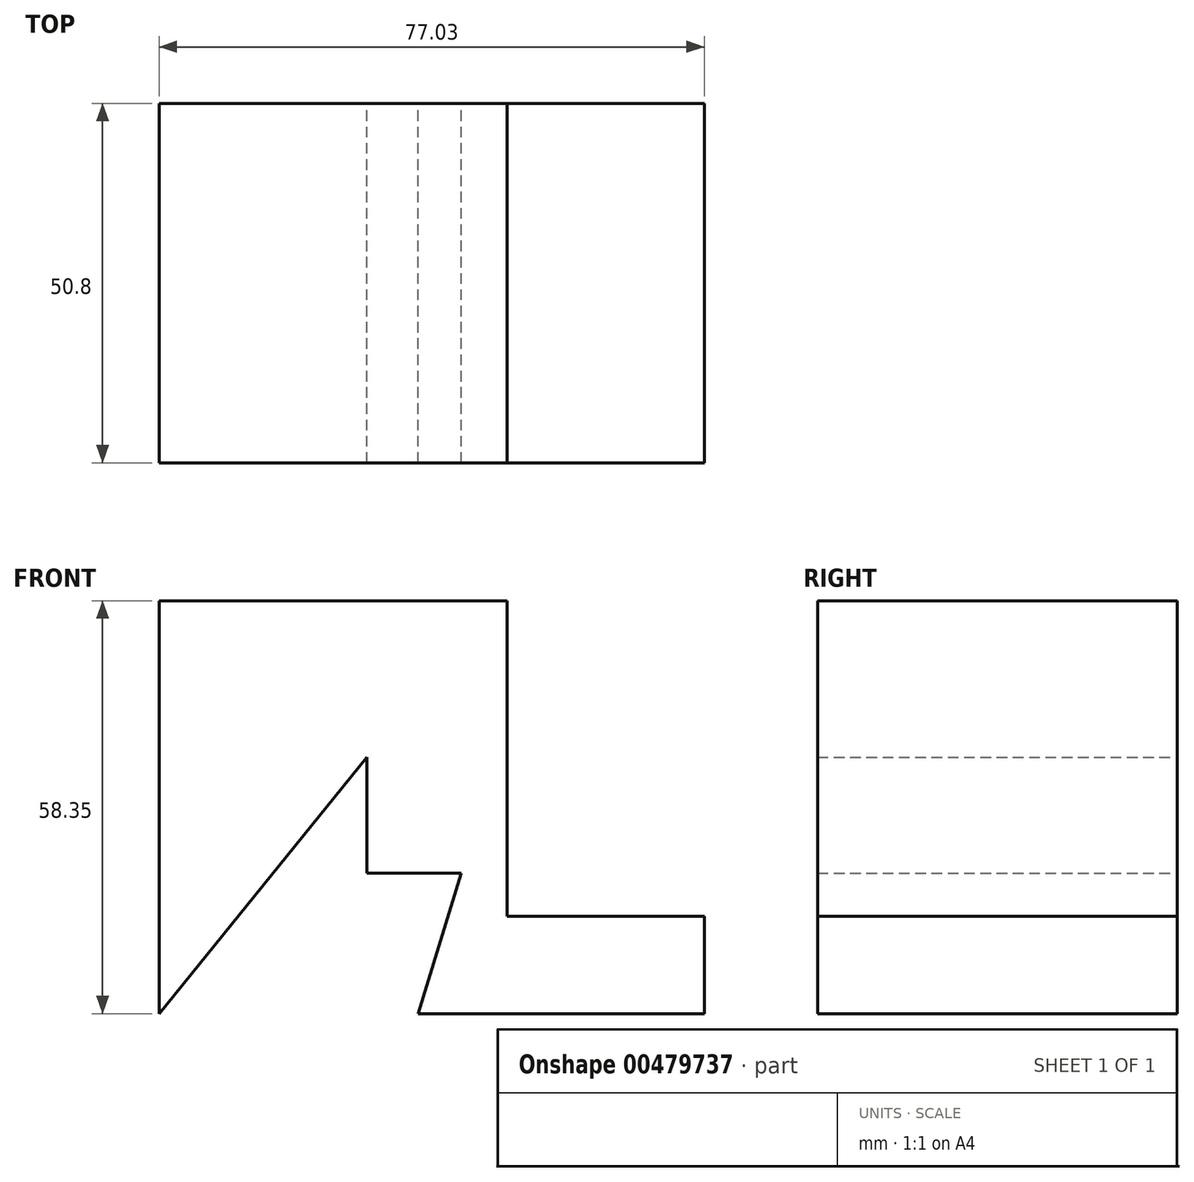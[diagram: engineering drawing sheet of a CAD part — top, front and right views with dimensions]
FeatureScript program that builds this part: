
annotation { "Feature Type Name" : "Feature", "Feature Type Description" : "" }
export const myFeature = defineFeature(function(context is Context, id is Id, definition is map)
    precondition{}
    {
        {
            var Q0;
            Q0=qCreatedBy(makeId("Front.planeOp"),FACE);
            var sketch = newSketch(context, id + "F0", { "sketchPlane" : qUnion([Q0])});
            skLineSegment(sketch, "E0", {"start": v(0, 0) * mm, "end": v(-36.6, 0) * mm});
            skLineSegment(sketch, "E1", {"start": v(-36.6, 0) * mm, "end": v(-30.5, 19.83) * mm});
            skLineSegment(sketch, "E2", {"start": v(-30.5, 19.83) * mm, "end": v(-43.86, 19.83) * mm});
            skLineSegment(sketch, "E3", {"start": v(-43.86, 19.83) * mm, "end": v(-43.86, 36.23) * mm});
            skLineSegment(sketch, "E4", {"start": v(-43.86, 36.23) * mm, "end": v(-73.22, 0) * mm});
            skLineSegment(sketch, "E5", {"start": v(-73.22, 0) * mm, "end": v(-73.22, 58.35) * mm});
            skLineSegment(sketch, "E6", {"start": v(-73.22, 58.35) * mm, "end": v(-24.03, 58.35) * mm});
            skLineSegment(sketch, "E7", {"start": v(-24.03, 58.35) * mm, "end": v(-24.03, 13.73) * mm});
            skLineSegment(sketch, "E8", {"start": v(-24.03, 13.73) * mm, "end": v(3.81, 13.73) * mm});
            skLineSegment(sketch, "E9", {"start": v(3.81, 13.73) * mm, "end": v(3.81, 0) * mm});
            skLineSegment(sketch, "E10", {"start": v(3.81, 0) * mm, "end": v(0, 0) * mm});
            skSolve(sketch);
        }
        {
            var Q0;
            Q0 = qSketchRegion(id + "F0", true);
            extrude(context, id + "F1", {"entities" : qUnion([Q0]), "depth" : 50.8 * mm});
        }
    });
